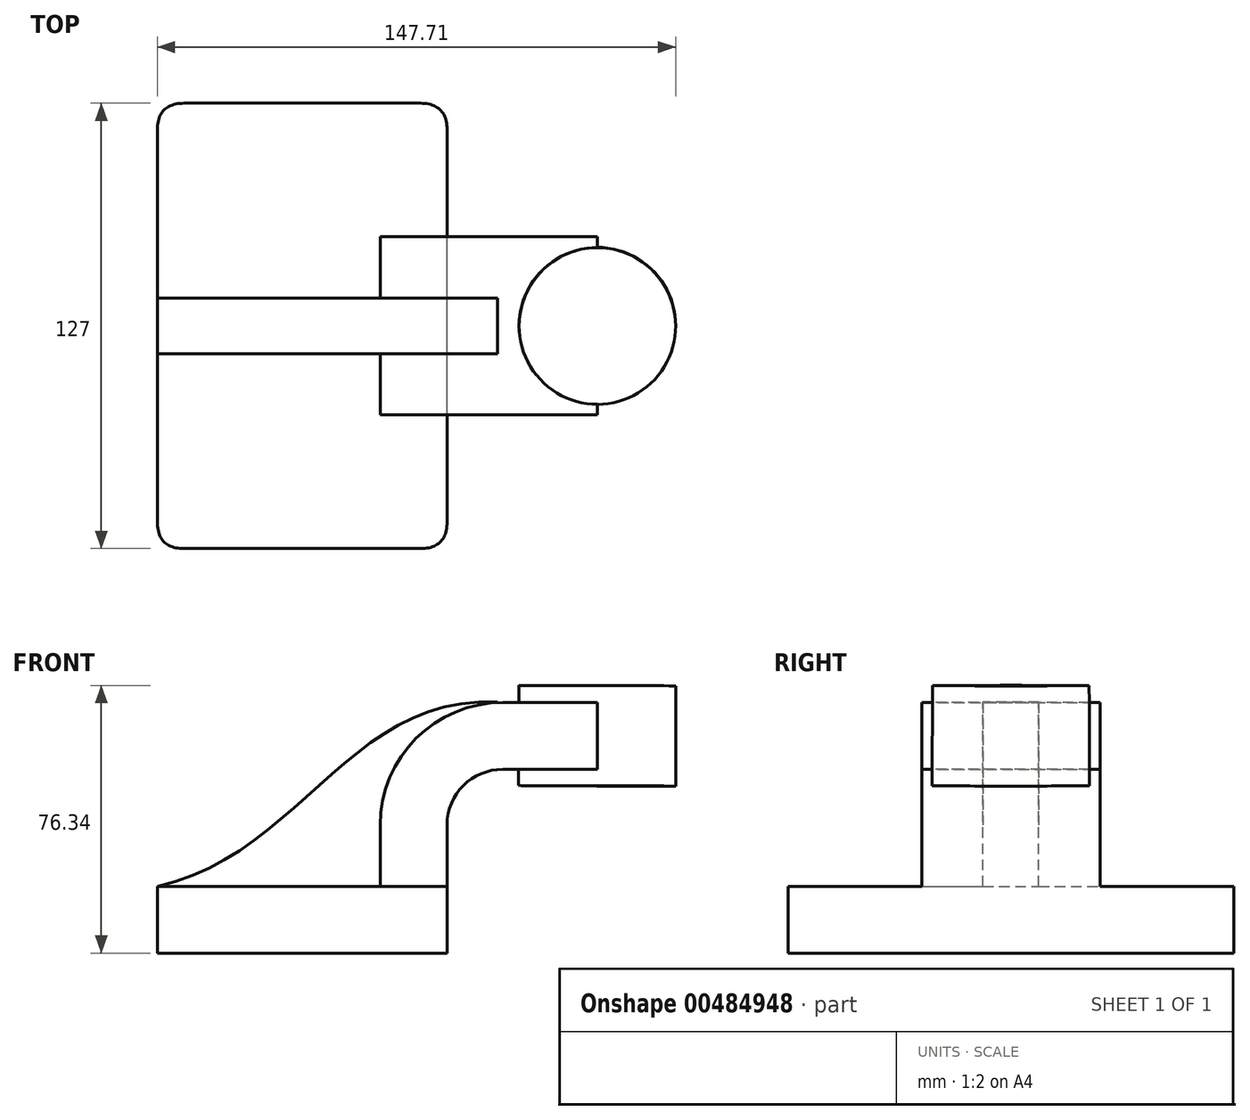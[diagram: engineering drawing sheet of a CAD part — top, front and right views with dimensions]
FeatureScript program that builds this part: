
annotation { "Feature Type Name" : "Feature", "Feature Type Description" : "" }
export const myFeature = defineFeature(function(context is Context, id is Id, definition is map)
    precondition{}
    {
        {
            var Q0;
            Q0=qCreatedBy(makeId("Front.planeOp"),FACE);
            var sketch = newSketch(context, id + "F0", { "sketchPlane" : qUnion([Q0])});
            skLineSegment(sketch, "E0.bottom", {"start": v(-41.28, -9.52) * mm, "end": v(41.28, -9.52) * mm});
            skLineSegment(sketch, "E0.top", {"start": v(-41.28, 9.53) * mm, "end": v(41.28, 9.53) * mm});
            skLineSegment(sketch, "E0.left", {"start": v(-41.28, -9.52) * mm, "end": v(-41.28, 9.53) * mm});
            skLineSegment(sketch, "E0.right", {"start": v(41.28, -9.53) * mm, "end": v(41.28, 9.52) * mm});
            skPoint(sketch, "E0.middle", {"position": v(0, 0) * mm});
            skLineSegment(sketch, "E1.bottom", {"start": v(55.63, 38.1) * mm, "end": v(106.43, 38.1) * mm});
            skLineSegment(sketch, "E1.top", {"start": v(55.63, 66.68) * mm, "end": v(106.43, 66.68) * mm});
            skLineSegment(sketch, "E1.left", {"start": v(55.63, 38.1) * mm, "end": v(55.63, 66.68) * mm});
            skLineSegment(sketch, "E1.right", {"start": v(106.43, 38.1) * mm, "end": v(106.43, 66.68) * mm});
            skPoint(sketch, "E1.middle", {"position": v(81.03, 52.39) * mm});
            skLineSegment(sketch, "E2", {"start": v(41.28, 9.52) * mm, "end": v(41.28, 27) * mm});
            skArc(sketch, "E3", {"start": v(41.28, 27) * mm, "mid": v(45.92, 38.23) * mm, "end": v(57.15, 42.88) * mm});
            skLineSegment(sketch, "E4", {"start": v(57.15, 42.88) * mm, "end": v(84.12, 42.88) * mm});
            skLineSegment(sketch, "E5.0", {"start": v(57.15, 61.93) * mm, "end": v(84.12, 61.93) * mm});
            skArc(sketch, "E5.1", {"start": v(22.23, 27) * mm, "mid": v(32.45, 51.7) * mm, "end": v(57.15, 61.93) * mm});
            skLineSegment(sketch, "E5.2", {"start": v(22.23, 9.52) * mm, "end": v(22.23, 27) * mm});
            skLineSegment(sketch, "E6", {"start": v(84.03, 38.1) * mm, "end": v(84.12, 66.68) * mm});
            skFitSpline(sketch, "E7", {"points": [v(-41.28, 9.53) * mm, v(57.15, 61.93) * mm], "startDerivative": vector(123.82, 26.9) * mm, "endDerivative": vector(130.33, -10.11) * mm});
            skSolve(sketch);
        }
        {
            var Q0;
            Q0=makeQuery(id+"F0.imprint","IMPRINT",FACE,{"disambiguationData":[TD([[makeQuery(id+"F0.imprint","IMPRINT",EDGE,{"derivedFrom":sQuery(id+"F0.wireOp",EDGE,"E0.bottom")}),1.0]])]});
            extrude(context, id + "F1", {"entities" : qUnion([Q0]), "endBound" : BoundingType.SYMMETRIC, "depth" : 127 * mm});
        }
        {
            var Q0;
            {var subQ0=sQuery(id+"F0.wireOp",EDGE,"E2");Q0=makeQuery(id+"F0.imprint","IMPRINT",FACE,{"disambiguationData":[TD([[makeQuery(id+"F0.imprint","IMPRINT",EDGE,{"derivedFrom":subQ0}),1.0]])]});}
            var Q1;
            {var subQ6=sQuery(id+"F0.wireOp",EDGE,"E3");var subQ9=sQuery(id+"F0.wireOp",EDGE,"E1.left");var subQ10=makeQuery(id+"F0.imprint","INTERSECT",VERTEX,{"derivedFrom":[subQ9,subQ6]});Q1=makeQuery(id+"F0.imprint","IMPRINT",FACE,{"disambiguationData":[TD([[makeQuery(id+"F0.imprint","IMPRINT",EDGE,{"disambiguationData":[TD([[subQ10,-1.0]])],"derivedFrom":subQ9}),-1.0]])]});}
            extrude(context, id + "F2", {"entities" : qUnion([Q0, Q1]), "operationType" : NewBodyOperationType.ADD, "endBound" : BoundingType.SYMMETRIC, "depth" : 50.8 * mm});
        }
        {
            var Q0;
            {var subQ0=sQuery(id+"F0.wireOp",EDGE,"E5.2");Q0=makeQuery(id+"F0.imprint","IMPRINT",FACE,{"disambiguationData":[TD([[makeQuery(id+"F0.imprint","IMPRINT",EDGE,{"derivedFrom":subQ0}),1.0]])]});}
            extrude(context, id + "F3", {"entities" : qUnion([Q0]), "operationType" : NewBodyOperationType.ADD, "endBound" : BoundingType.SYMMETRIC, "depth" : 15.88 * mm});
        }
        {
            var Q0;
            {var subQ4=sQuery(id+"F0.wireOp",EDGE,"E1.right");Q0=makeQuery(id+"F0.imprint","IMPRINT",FACE,{"disambiguationData":[TD([[makeQuery(id+"F0.imprint","IMPRINT",EDGE,{"derivedFrom":subQ4}),1.0]])]});}
            var Q1;
            Q1=sQuery(id+"F0.wireOp",EDGE,"E6");
            revolve(context, id + "F4", {"operationType" : NewBodyOperationType.ADD, "entities" : qUnion([Q0]), "axis" : qUnion([Q1]), "revolveType" : RevolveType.FULL});
        }
        {
            var Q0;
            Q0=makeQuery(id+"F1.opExtrude","CAP_EDGE",EDGE,{"disambiguationData":[OSD([sQuery(id+"F0.wireOp",EDGE,"E0.left")])],"isStart":false});
            var Q1;
            Q1=makeQuery(id+"F1.opExtrude","CAP_EDGE",EDGE,{"disambiguationData":[OSD([sQuery(id+"F0.wireOp",EDGE,"E0.right")])],"isStart":false});
            var Q2;
            Q2=makeQuery(id+"F1.opExtrude","CAP_EDGE",EDGE,{"disambiguationData":[OSD([sQuery(id+"F0.wireOp",EDGE,"E0.left")])],"isStart":true});
            var Q3;
            Q3=makeQuery(id+"F1.opExtrude","CAP_EDGE",EDGE,{"disambiguationData":[OSD([sQuery(id+"F0.wireOp",EDGE,"E0.right")])],"isStart":true});
            fillet(context, id + "F5", {"entities" : qUnion([Q0, Q1, Q2, Q3]), "radius" : 7.62 * mm, "tangentPropagation" : true, "rho" : 0.5, "crossSection" : FilletCrossSection.CONIC, "allowEdgeOverflow" : false});
        }
    });
